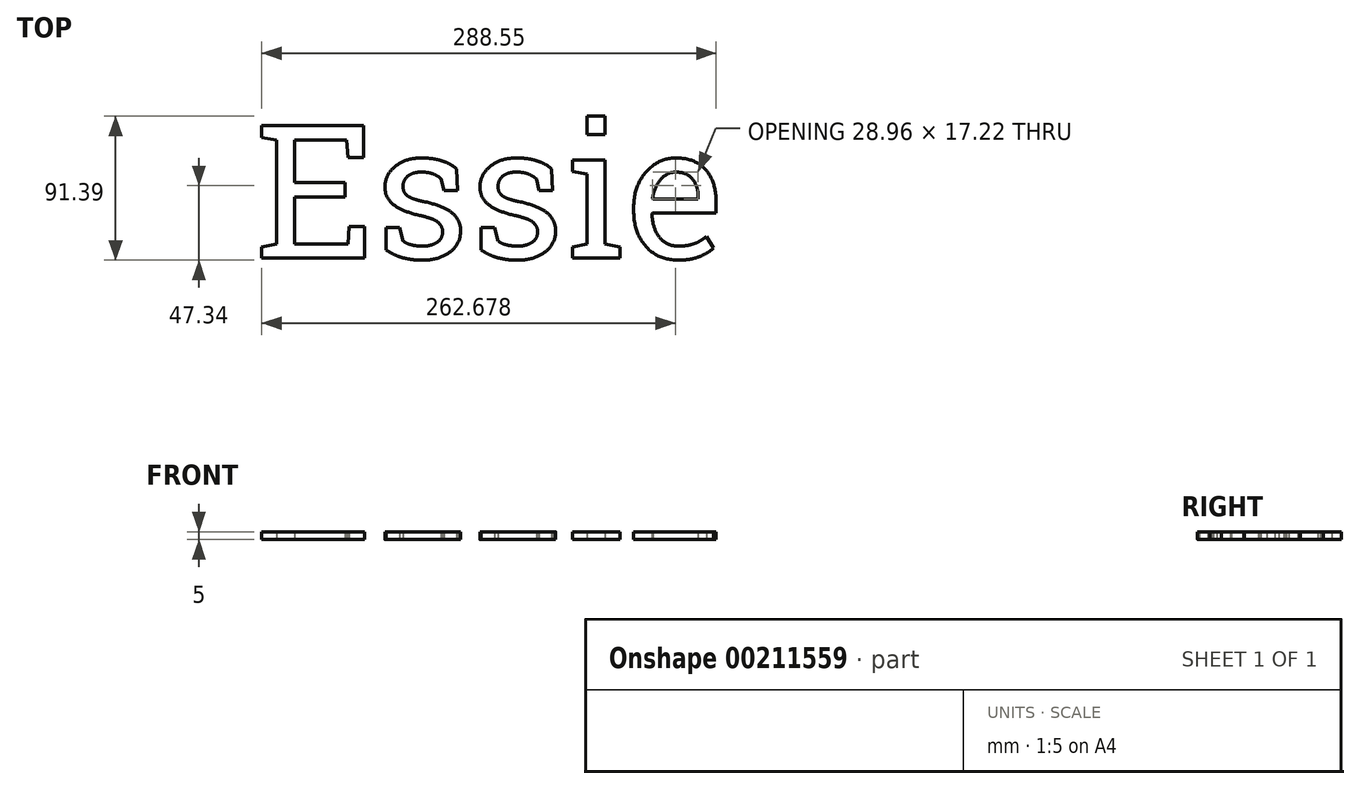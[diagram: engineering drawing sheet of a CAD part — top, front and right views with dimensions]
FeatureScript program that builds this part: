
annotation { "Feature Type Name" : "Feature", "Feature Type Description" : "" }
export const myFeature = defineFeature(function(context is Context, id is Id, definition is map)
    precondition{}
    {
        {
            var Q0;
            Q0=qCreatedBy(makeId("Top.planeOp"),FACE);
            var sketch = newSketch(context, id + "F0", { "sketchPlane" : qUnion([Q0])});
            skText(sketch, "E0", { "text": "Essie", "fontName": "RobotoSlab-Regular.ttf"});
            const initialGuessF0  = {"E0": [-0.09183, -0.04422, 1, 0, 0.08523]};
            skSetInitialGuess(sketch, initialGuessF0);
            skSolve(sketch);
        }
        {
            var Q0;
            Q0 = qSketchRegion(id + "F0", true);
            extrude(context, id + "F1", {"entities" : qUnion([Q0]), "depth" : 5 * mm});
        }
    });
